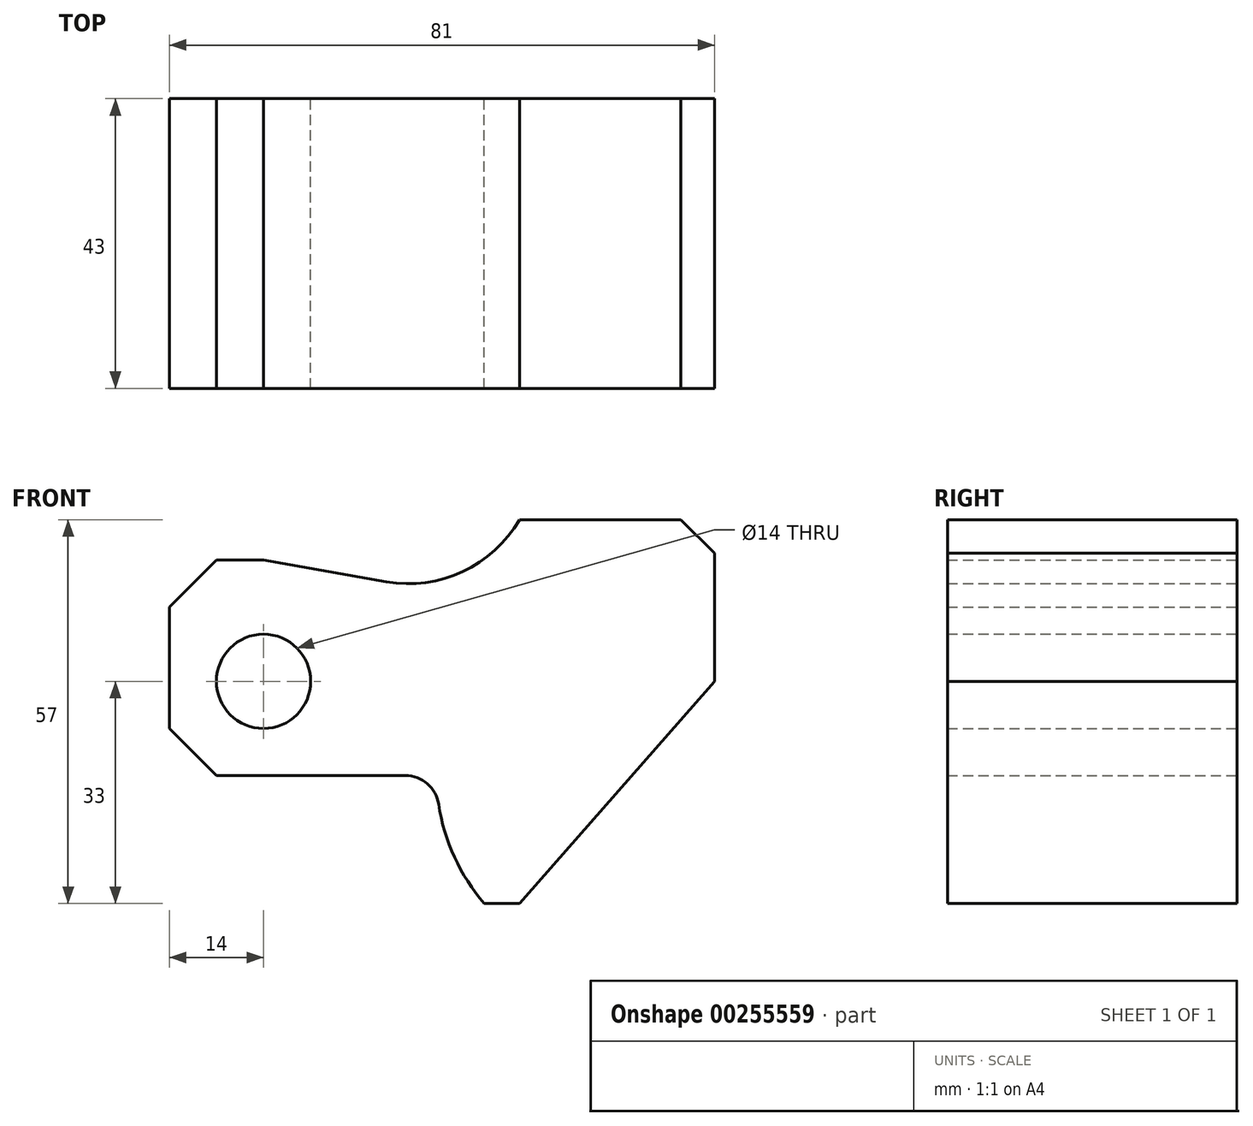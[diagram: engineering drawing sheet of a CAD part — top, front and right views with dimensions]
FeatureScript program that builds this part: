
annotation { "Feature Type Name" : "Feature", "Feature Type Description" : "" }
export const myFeature = defineFeature(function(context is Context, id is Id, definition is map)
    precondition{}
    {
        {
            var Q0;
            Q0=qCreatedBy(makeId("Front.planeOp"),FACE);
            var sketch = newSketch(context, id + "F0", { "sketchPlane" : qUnion([Q0])});
            skLineSegment(sketch, "E0.top", {"start": v(62, 24) * mm, "end": v(38, 24) * mm});
            skLineSegment(sketch, "E0.left", {"start": v(67, 0) * mm, "end": v(67, 19) * mm});
            skPoint(sketch, "E1.start.orphan", {"position": v(67, 24) * mm});
            skLineSegment(sketch, "E2", {"start": v(67, 19) * mm, "end": v(62, 24) * mm});
            skLineSegment(sketch, "E3", {"start": v(67, 0) * mm, "end": v(38, -33) * mm});
            skLineSegment(sketch, "E4", {"start": v(38, -33) * mm, "end": v(70.34, -33) * mm, "construction": true});
            skPoint(sketch, "E5", {"position": v(54.7, -14) * mm});
            skArc(sketch, "E6", {"start": v(26.01, -18.26) * mm, "mid": v(28.35, -26.12) * mm, "end": v(32.79, -33) * mm});
            skLineSegment(sketch, "E7", {"start": v(38, -33) * mm, "end": v(32.79, -33) * mm, "construction": true});
            skLineSegment(sketch, "E8", {"start": v(67, 24) * mm, "end": v(38, 24) * mm, "construction": true});
            skArc(sketch, "E9", {"start": v(18.24, 14.78) * mm, "mid": v(29.57, 16.28) * mm, "end": v(38, 24) * mm});
            skLineSegment(sketch, "E10", {"start": v(32.79, -33) * mm, "end": v(38, -33) * mm});
            skPoint(sketch, "E11.orphan", {"position": v(-42.03, -33) * mm});
            skPoint(sketch, "E12.start.orphan", {"position": v(-26.5, -33) * mm});
            skPoint(sketch, "E13.orphan", {"position": v(-4.7, -33) * mm});
            skLineSegment(sketch, "E14", {"start": v(-14, -7) * mm, "end": v(-7, -14) * mm});
            skPoint(sketch, "E15", {"position": v(-14, 18) * mm});
            skPoint(sketch, "E16.end.orphan", {"position": v(-42.03, -14) * mm});
            skLineSegment(sketch, "E17", {"start": v(-7, 18) * mm, "end": v(0, 18) * mm});
            skPoint(sketch, "E18", {"position": v(-14, 11) * mm});
            skLineSegment(sketch, "E19", {"start": v(-14, 11) * mm, "end": v(-7, 18) * mm});
            skLineSegment(sketch, "E20", {"start": v(18.24, 14.78) * mm, "end": v(0, 18) * mm});
            skLineSegment(sketch, "E21", {"start": v(-7, 18) * mm, "end": v(0, 18) * mm, "construction": true});
            skArc(sketch, "E22", {"start": v(26.01, -18.26) * mm, "mid": v(24.33, -15.21) * mm, "end": v(21.07, -14) * mm});
            skCircle(sketch, "E23", {"center": v(0, 0) * mm, "radius": 7 * mm});
            skPoint(sketch, "E24", {"position": v(62, 24) * mm});
            skLineSegment(sketch, "E25", {"start": v(-14, -7) * mm, "end": v(-14, 11) * mm});
            skLineSegment(sketch, "E26", {"start": v(21.07, -14) * mm, "end": v(-7, -14) * mm});
            skLineSegment(sketch, "E27", {"start": v(70.34, -33) * mm, "end": v(-42.03, -33) * mm, "construction": true});
            skSolve(sketch);
        }
        {
            var Q0;
            Q0=makeQuery(id+"F0.imprint","IMPRINT",FACE,{"disambiguationData":[TD([[makeQuery(id+"F0.imprint","IMPRINT",EDGE,{"derivedFrom":sQuery(id+"F0.wireOp",EDGE,"E0.top")}),1.0]])]});
            extrude(context, id + "F1", {"entities" : qUnion([Q0]), "endBound" : BoundingType.SYMMETRIC, "depth" : 43 * mm});
        }
    });
